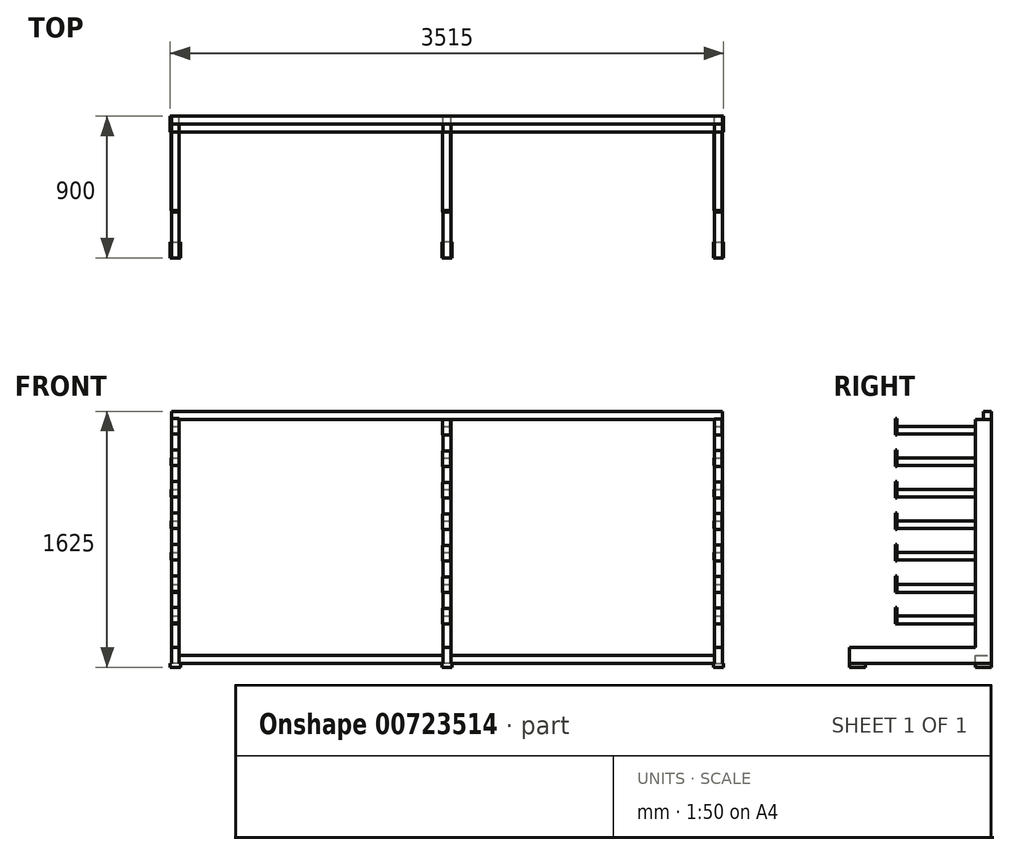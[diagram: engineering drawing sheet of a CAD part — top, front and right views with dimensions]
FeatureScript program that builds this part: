
annotation { "Feature Type Name" : "Feature", "Feature Type Description" : "" }
export const myFeature = defineFeature(function(context is Context, id is Id, definition is map)
    precondition{}
    {
        {
            var Q0;
            Q0=qCreatedBy(makeId("Front.planeOp"),FACE);
            var sketch = newSketch(context, id + "F0", { "sketchPlane" : qUnion([Q0])});
            skLineSegment(sketch, "E0.bottom", {"start": v(0, 0) * mm, "end": v(-3500, 0) * mm});
            skLineSegment(sketch, "E0.left", {"start": v(0, 0) * mm, "end": v(0, 1550) * mm});
            skLineSegment(sketch, "E0.right", {"start": v(-3500, 0) * mm, "end": v(-3500, 1550) * mm});
            skLineSegment(sketch, "E1.1", {"start": v(-50, 50) * mm, "end": v(-50, 1550) * mm});
            skLineSegment(sketch, "E1.2", {"start": v(-50, 50) * mm, "end": v(-1725, 50) * mm});
            skLineSegment(sketch, "E1.3", {"start": v(-3450, 50) * mm, "end": v(-3450, 1550) * mm});
            skPoint(sketch, "E2", {"position": v(-1775, 50) * mm});
            skPoint(sketch, "E3", {"position": v(-1725, 50) * mm});
            skLineSegment(sketch, "E4", {"start": v(-1775, 50) * mm, "end": v(-1775, 1550) * mm});
            skLineSegment(sketch, "E5.0", {"start": v(-1725, 50) * mm, "end": v(-1725, 1550) * mm});
            skLineSegment(sketch, "E6.trimOffspring", {"start": v(-1775, 50) * mm, "end": v(-3450, 50) * mm});
            skLineSegment(sketch, "E7", {"start": v(-3450, 1550) * mm, "end": v(-3500, 1550) * mm});
            skLineSegment(sketch, "E8", {"start": v(-1775, 1550) * mm, "end": v(-1725, 1550) * mm});
            skLineSegment(sketch, "E9", {"start": v(-50, 1550) * mm, "end": v(0, 1550) * mm});
            skSolve(sketch);
        }
        {
            var Q0;
            Q0=makeQuery(id+"F0.imprint","IMPRINT",FACE,{"disambiguationData":[TD([[makeQuery(id+"F0.imprint","IMPRINT",EDGE,{"derivedFrom":sQuery(id+"F0.wireOp",EDGE,"E0.bottom")}),-1.0]])]});
            extrude(context, id + "F1", {"entities" : qUnion([Q0]), "depth" : 100 * mm, "offsetDistance" : 25 * mm});
        }
        {
            var Q0;
            Q0=makeQuery(id+"F1.opExtrude","CAP_FACE",FACE,{"disambiguationData":[OSD([sQuery(id+"F0.wireOp",EDGE,"E0.bottom"),sQuery(id+"F0.wireOp",EDGE,"E0.left"),sQuery(id+"F0.wireOp",EDGE,"E0.right"),sQuery(id+"F0.wireOp",EDGE,"E1.1"),sQuery(id+"F0.wireOp",EDGE,"E1.2"),sQuery(id+"F0.wireOp",EDGE,"E1.3"),sQuery(id+"F0.wireOp",EDGE,"E4"),sQuery(id+"F0.wireOp",EDGE,"E5.0"),sQuery(id+"F0.wireOp",EDGE,"E6.trimOffspring"),sQuery(id+"F0.wireOp",EDGE,"E7"),sQuery(id+"F0.wireOp",EDGE,"E8"),sQuery(id+"F0.wireOp",EDGE,"E9")])],"isStart":false});
            var sketch = newSketch(context, id + "F2", { "sketchPlane" : qUnion([Q0])});
            skLineSegment(sketch, "E10.bottom", {"start": v(-3500, 0) * mm, "end": v(-3450, 0) * mm});
            skLineSegment(sketch, "E10.top", {"start": v(-3500, 100) * mm, "end": v(-3450, 100) * mm});
            skLineSegment(sketch, "E10.left", {"start": v(-3500, 0) * mm, "end": v(-3500, 100) * mm});
            skLineSegment(sketch, "E10.right", {"start": v(-3450, 0) * mm, "end": v(-3450, 100) * mm});
            skLineSegment(sketch, "E11.bottom", {"start": v(-1775, 0) * mm, "end": v(-1725, 0) * mm});
            skLineSegment(sketch, "E11.top", {"start": v(-1775, 100) * mm, "end": v(-1725, 100) * mm});
            skLineSegment(sketch, "E11.left", {"start": v(-1775, 0) * mm, "end": v(-1775, 100) * mm});
            skLineSegment(sketch, "E11.right", {"start": v(-1725, 0) * mm, "end": v(-1725, 100) * mm});
            skLineSegment(sketch, "E12.bottom", {"start": v(0, 0) * mm, "end": v(-50, 0) * mm});
            skLineSegment(sketch, "E12.top", {"start": v(0, 100) * mm, "end": v(-50, 100) * mm});
            skLineSegment(sketch, "E12.left", {"start": v(0, 0) * mm, "end": v(0, 100) * mm});
            skLineSegment(sketch, "E12.right", {"start": v(-50, 0) * mm, "end": v(-50, 100) * mm});
            skSolve(sketch);
        }
        {
            var Q0;
            {var subQ2=sQuery(id+"F2.wireOp",EDGE,"E11.bottom");Q0=makeQuery(id+"F2.imprint","IMPRINT",FACE,{"disambiguationData":[TD([[makeQuery(id+"F2.imprint","IMPRINT",EDGE,{"derivedFrom":subQ2}),-1.0]])]});}
            var Q1;
            {var subQ3=sQuery(id+"F2.wireOp",EDGE,"E10.bottom");Q1=makeQuery(id+"F2.imprint","IMPRINT",FACE,{"disambiguationData":[TD([[makeQuery(id+"F2.imprint","IMPRINT",EDGE,{"derivedFrom":subQ3}),-1.0]])]});}
            var Q2;
            {var subQ3=sQuery(id+"F2.wireOp",EDGE,"E12.bottom");Q2=makeQuery(id+"F2.imprint","IMPRINT",FACE,{"disambiguationData":[TD([[makeQuery(id+"F2.imprint","IMPRINT",EDGE,{"derivedFrom":subQ3}),-1.0]])]});}
            extrude(context, id + "F3", {"entities" : qUnion([Q0, Q1, Q2]), "operationType" : NewBodyOperationType.ADD, "depth" : 800 * mm, "offsetDistance" : 25 * mm});
        }
        {
            var Q0;
            Q0=makeQuery(id+"F1.opExtrude","SWEPT_FACE",FACE,{"disambiguationData":[OSD([sQuery(id+"F0.wireOp",EDGE,"E8")])]});
            var sketch = newSketch(context, id + "F4", { "sketchPlane" : qUnion([Q0])});
            skPoint(sketch, "E13", {"position": v(-1750, 0) * mm});
            skPoint(sketch, "E14", {"position": v(-1750, -100) * mm});
            skLineSegment(sketch, "E15", {"start": v(-1750, 0) * mm, "end": v(-1750, -50) * mm});
            skLineSegment(sketch, "E16.bottom", {"start": v(-1750, -50) * mm, "end": v(-3499.82, -50) * mm});
            skLineSegment(sketch, "E16.top", {"start": v(-1750, 0) * mm, "end": v(-3499.82, 0) * mm});
            skLineSegment(sketch, "E16.left", {"start": v(-1750, -50) * mm, "end": v(-1750, 0) * mm});
            skLineSegment(sketch, "E16.right", {"start": v(-3499.82, -50) * mm, "end": v(-3499.82, 0) * mm});
            skLineSegment(sketch, "E17.MirrorCS", {"start": v(-1750, 0) * mm, "end": v(-0.18, 0) * mm});
            skLineSegment(sketch, "E18.MirrorCS", {"start": v(-1750, -50) * mm, "end": v(-0.18, -50) * mm});
            skLineSegment(sketch, "E19.MirrorCS", {"start": v(-0.18, -50) * mm, "end": v(-0.18, 0) * mm});
            skSolve(sketch);
        }
        {
            var Q0;
            Q0 = qSketchRegion(id + "F4", true);
            extrude(context, id + "F5", {"entities" : qUnion([Q0]), "operationType" : NewBodyOperationType.ADD, "depth" : 50 * mm, "offsetDistance" : 25 * mm});
        }
        {
            var Q0;
            {var subQ0=sQuery(id+"F0.wireOp",EDGE,"E0.right");var subQ1=sQuery(id+"F0.wireOp",EDGE,"E7");var subQ2=sQuery(id+"F0.wireOp",EDGE,"E1.3");Q0=makeQuery(id+"F3.boolean.opBoolean","SPLIT",FACE,{"disambiguationData":[TD([makeQuery(id+"F1.opExtrude","SWEPT_FACE",FACE,{"disambiguationData":[OSD([subQ0])]})])],"derivedFrom":makeQuery(id+"F1.opExtrude","CAP_FACE",FACE,{"disambiguationData":[OSD([sQuery(id+"F0.wireOp",EDGE,"E0.bottom"),sQuery(id+"F0.wireOp",EDGE,"E0.left"),subQ0,sQuery(id+"F0.wireOp",EDGE,"E1.1"),sQuery(id+"F0.wireOp",EDGE,"E1.2"),subQ2,sQuery(id+"F0.wireOp",EDGE,"E4"),sQuery(id+"F0.wireOp",EDGE,"E5.0"),sQuery(id+"F0.wireOp",EDGE,"E6.trimOffspring"),subQ1,sQuery(id+"F0.wireOp",EDGE,"E8"),sQuery(id+"F0.wireOp",EDGE,"E9")])],"isStart":false})});}
            var sketch = newSketch(context, id + "F6", { "sketchPlane" : qUnion([Q0])});
            skLineSegment(sketch, "E20.bottom", {"start": v(-3500, 250) * mm, "end": v(-3450, 250) * mm});
            skLineSegment(sketch, "E20.top", {"start": v(-3500, 300) * mm, "end": v(-3450, 300) * mm});
            skLineSegment(sketch, "E20.left", {"start": v(-3500, 250) * mm, "end": v(-3500, 300) * mm});
            skLineSegment(sketch, "E20.right", {"start": v(-3450, 250) * mm, "end": v(-3450, 300) * mm});
            skPoint(sketch, "E21", {"position": v(-3500, 450) * mm});
            skLineSegment(sketch, "E22.bottom", {"start": v(-3500, 450) * mm, "end": v(-3450, 450) * mm});
            skLineSegment(sketch, "E22.top", {"start": v(-3500, 500) * mm, "end": v(-3450, 500) * mm});
            skLineSegment(sketch, "E22.left", {"start": v(-3500, 450) * mm, "end": v(-3500, 500) * mm});
            skLineSegment(sketch, "E22.right", {"start": v(-3450, 450) * mm, "end": v(-3450, 500) * mm});
            skPoint(sketch, "E23", {"position": v(-3500, 650) * mm});
            skPoint(sketch, "E24", {"position": v(-3500.84, 655.24) * mm});
            skPoint(sketch, "E25", {"position": v(-3500.84, 855.24) * mm});
            skPoint(sketch, "E26", {"position": v(-3500.84, 1055.24) * mm});
            skPoint(sketch, "E27", {"position": v(-3500.84, 1255.24) * mm});
            skLineSegment(sketch, "E28.bottom", {"start": v(-3500.84, 655.24) * mm, "end": v(-3450.84, 655.24) * mm});
            skLineSegment(sketch, "E28.top", {"start": v(-3500.84, 705.24) * mm, "end": v(-3450.84, 705.24) * mm});
            skLineSegment(sketch, "E28.left", {"start": v(-3500.84, 655.24) * mm, "end": v(-3500.84, 705.24) * mm});
            skLineSegment(sketch, "E28.right", {"start": v(-3450.84, 655.24) * mm, "end": v(-3450.84, 705.24) * mm});
            skLineSegment(sketch, "E29.bottom", {"start": v(-3500.84, 855.24) * mm, "end": v(-3450.84, 855.24) * mm});
            skLineSegment(sketch, "E29.top", {"start": v(-3500.84, 905.24) * mm, "end": v(-3450.84, 905.24) * mm});
            skLineSegment(sketch, "E29.left", {"start": v(-3500.84, 855.24) * mm, "end": v(-3500.84, 905.24) * mm});
            skLineSegment(sketch, "E29.right", {"start": v(-3450.84, 855.24) * mm, "end": v(-3450.84, 905.24) * mm});
            skLineSegment(sketch, "E30.bottom", {"start": v(-3500.84, 1055.24) * mm, "end": v(-3450.84, 1055.24) * mm});
            skLineSegment(sketch, "E30.top", {"start": v(-3500.84, 1105.24) * mm, "end": v(-3450.84, 1105.24) * mm});
            skLineSegment(sketch, "E30.left", {"start": v(-3500.84, 1055.24) * mm, "end": v(-3500.84, 1105.24) * mm});
            skLineSegment(sketch, "E30.right", {"start": v(-3450.84, 1055.24) * mm, "end": v(-3450.84, 1105.24) * mm});
            skLineSegment(sketch, "E31.bottom", {"start": v(-3500.84, 1255.24) * mm, "end": v(-3450.84, 1255.24) * mm});
            skLineSegment(sketch, "E31.top", {"start": v(-3500.84, 1305.24) * mm, "end": v(-3450.84, 1305.24) * mm});
            skLineSegment(sketch, "E31.left", {"start": v(-3500.84, 1255.24) * mm, "end": v(-3500.84, 1305.24) * mm});
            skLineSegment(sketch, "E31.right", {"start": v(-3450.84, 1255.24) * mm, "end": v(-3450.84, 1305.24) * mm});
            skPoint(sketch, "E32", {"position": v(-3500, 1455.24) * mm});
            skLineSegment(sketch, "E33.bottom", {"start": v(-3500, 1455.24) * mm, "end": v(-3450, 1455.24) * mm});
            skLineSegment(sketch, "E33.top", {"start": v(-3500, 1505.24) * mm, "end": v(-3450, 1505.24) * mm});
            skLineSegment(sketch, "E33.left", {"start": v(-3500, 1455.24) * mm, "end": v(-3500, 1505.24) * mm});
            skLineSegment(sketch, "E33.right", {"start": v(-3450, 1455.24) * mm, "end": v(-3450, 1505.24) * mm});
            skPoint(sketch, "E34", {"position": v(-52.24, 250) * mm});
            skPoint(sketch, "E35", {"position": v(-1777.89, 250) * mm});
            skLineSegment(sketch, "E36.bottom", {"start": v(-1777.89, 250) * mm, "end": v(-1727.89, 250) * mm});
            skLineSegment(sketch, "E36.top", {"start": v(-1777.89, 300) * mm, "end": v(-1727.89, 300) * mm});
            skLineSegment(sketch, "E36.left", {"start": v(-1777.89, 250) * mm, "end": v(-1777.89, 300) * mm});
            skLineSegment(sketch, "E36.right", {"start": v(-1727.89, 250) * mm, "end": v(-1727.89, 300) * mm});
            skPoint(sketch, "E37", {"position": v(-1777.89, 450) * mm});
            skLineSegment(sketch, "E38.bottom", {"start": v(-1777.89, 450) * mm, "end": v(-1727.89, 450) * mm});
            skLineSegment(sketch, "E38.top", {"start": v(-1777.89, 500) * mm, "end": v(-1727.89, 500) * mm});
            skLineSegment(sketch, "E38.left", {"start": v(-1777.89, 450) * mm, "end": v(-1777.89, 500) * mm});
            skLineSegment(sketch, "E38.right", {"start": v(-1727.89, 450) * mm, "end": v(-1727.89, 500) * mm});
            skPoint(sketch, "E39", {"position": v(-1777.89, 650) * mm});
            skPoint(sketch, "E40", {"position": v(-1778.73, 655.24) * mm});
            skPoint(sketch, "E41", {"position": v(-1778.73, 855.24) * mm});
            skPoint(sketch, "E42", {"position": v(-1778.73, 1055.24) * mm});
            skPoint(sketch, "E43", {"position": v(-1778.73, 1255.24) * mm});
            skLineSegment(sketch, "E44.bottom", {"start": v(-1778.73, 655.24) * mm, "end": v(-1728.73, 655.24) * mm});
            skLineSegment(sketch, "E44.top", {"start": v(-1778.73, 705.24) * mm, "end": v(-1728.73, 705.24) * mm});
            skLineSegment(sketch, "E44.left", {"start": v(-1778.73, 655.24) * mm, "end": v(-1778.73, 705.24) * mm});
            skLineSegment(sketch, "E44.right", {"start": v(-1728.73, 655.24) * mm, "end": v(-1728.73, 705.24) * mm});
            skLineSegment(sketch, "E45.bottom", {"start": v(-1778.73, 855.24) * mm, "end": v(-1728.73, 855.24) * mm});
            skLineSegment(sketch, "E45.top", {"start": v(-1778.73, 905.24) * mm, "end": v(-1728.73, 905.24) * mm});
            skLineSegment(sketch, "E45.left", {"start": v(-1778.73, 855.24) * mm, "end": v(-1778.73, 905.24) * mm});
            skLineSegment(sketch, "E45.right", {"start": v(-1728.73, 855.24) * mm, "end": v(-1728.73, 905.24) * mm});
            skLineSegment(sketch, "E46.bottom", {"start": v(-1778.73, 1055.24) * mm, "end": v(-1728.73, 1055.24) * mm});
            skLineSegment(sketch, "E46.top", {"start": v(-1778.73, 1105.24) * mm, "end": v(-1728.73, 1105.24) * mm});
            skLineSegment(sketch, "E46.left", {"start": v(-1778.73, 1055.24) * mm, "end": v(-1778.73, 1105.24) * mm});
            skLineSegment(sketch, "E46.right", {"start": v(-1728.73, 1055.24) * mm, "end": v(-1728.73, 1105.24) * mm});
            skLineSegment(sketch, "E47.bottom", {"start": v(-1778.73, 1255.24) * mm, "end": v(-1728.73, 1255.24) * mm});
            skLineSegment(sketch, "E47.top", {"start": v(-1778.73, 1305.24) * mm, "end": v(-1728.73, 1305.24) * mm});
            skLineSegment(sketch, "E47.left", {"start": v(-1778.73, 1255.24) * mm, "end": v(-1778.73, 1305.24) * mm});
            skLineSegment(sketch, "E47.right", {"start": v(-1728.73, 1255.24) * mm, "end": v(-1728.73, 1305.24) * mm});
            skPoint(sketch, "E48", {"position": v(-1777.89, 1455.24) * mm});
            skLineSegment(sketch, "E49.bottom", {"start": v(-1777.89, 1455.24) * mm, "end": v(-1727.89, 1455.24) * mm});
            skLineSegment(sketch, "E49.top", {"start": v(-1777.89, 1505.24) * mm, "end": v(-1727.89, 1505.24) * mm});
            skLineSegment(sketch, "E49.left", {"start": v(-1777.89, 1455.24) * mm, "end": v(-1777.89, 1505.24) * mm});
            skLineSegment(sketch, "E49.right", {"start": v(-1727.89, 1455.24) * mm, "end": v(-1727.89, 1505.24) * mm});
            skLineSegment(sketch, "E50.bottom", {"start": v(-52.24, 250) * mm, "end": v(-2.24, 250) * mm});
            skLineSegment(sketch, "E50.top", {"start": v(-52.24, 300) * mm, "end": v(-2.24, 300) * mm});
            skLineSegment(sketch, "E50.left", {"start": v(-52.24, 250) * mm, "end": v(-52.24, 300) * mm});
            skLineSegment(sketch, "E50.right", {"start": v(-2.24, 250) * mm, "end": v(-2.24, 300) * mm});
            skPoint(sketch, "E51", {"position": v(-52.24, 450) * mm});
            skLineSegment(sketch, "E52.bottom", {"start": v(-52.24, 450) * mm, "end": v(-2.24, 450) * mm});
            skLineSegment(sketch, "E52.top", {"start": v(-52.24, 500) * mm, "end": v(-2.24, 500) * mm});
            skLineSegment(sketch, "E52.left", {"start": v(-52.24, 450) * mm, "end": v(-52.24, 500) * mm});
            skLineSegment(sketch, "E52.right", {"start": v(-2.24, 450) * mm, "end": v(-2.24, 500) * mm});
            skPoint(sketch, "E53", {"position": v(-52.24, 650) * mm});
            skPoint(sketch, "E54", {"position": v(-53.08, 655.24) * mm});
            skPoint(sketch, "E55", {"position": v(-53.08, 855.24) * mm});
            skPoint(sketch, "E56", {"position": v(-53.08, 1055.24) * mm});
            skPoint(sketch, "E57", {"position": v(-53.08, 1255.24) * mm});
            skLineSegment(sketch, "E58.bottom", {"start": v(-53.08, 655.24) * mm, "end": v(-3.08, 655.24) * mm});
            skLineSegment(sketch, "E58.top", {"start": v(-53.08, 705.24) * mm, "end": v(-3.08, 705.24) * mm});
            skLineSegment(sketch, "E58.left", {"start": v(-53.08, 655.24) * mm, "end": v(-53.08, 705.24) * mm});
            skLineSegment(sketch, "E58.right", {"start": v(-3.08, 655.24) * mm, "end": v(-3.08, 705.24) * mm});
            skLineSegment(sketch, "E59.bottom", {"start": v(-53.08, 855.24) * mm, "end": v(-3.08, 855.24) * mm});
            skLineSegment(sketch, "E59.top", {"start": v(-53.08, 905.24) * mm, "end": v(-3.08, 905.24) * mm});
            skLineSegment(sketch, "E59.left", {"start": v(-53.08, 855.24) * mm, "end": v(-53.08, 905.24) * mm});
            skLineSegment(sketch, "E59.right", {"start": v(-3.08, 855.24) * mm, "end": v(-3.08, 905.24) * mm});
            skLineSegment(sketch, "E60.bottom", {"start": v(-53.08, 1055.24) * mm, "end": v(-3.08, 1055.24) * mm});
            skLineSegment(sketch, "E60.top", {"start": v(-53.08, 1105.24) * mm, "end": v(-3.08, 1105.24) * mm});
            skLineSegment(sketch, "E60.left", {"start": v(-53.08, 1055.24) * mm, "end": v(-53.08, 1105.24) * mm});
            skLineSegment(sketch, "E60.right", {"start": v(-3.08, 1055.24) * mm, "end": v(-3.08, 1105.24) * mm});
            skLineSegment(sketch, "E61.bottom", {"start": v(-53.08, 1255.24) * mm, "end": v(-3.08, 1255.24) * mm});
            skLineSegment(sketch, "E61.top", {"start": v(-53.08, 1305.24) * mm, "end": v(-3.08, 1305.24) * mm});
            skLineSegment(sketch, "E61.left", {"start": v(-53.08, 1255.24) * mm, "end": v(-53.08, 1305.24) * mm});
            skLineSegment(sketch, "E61.right", {"start": v(-3.08, 1255.24) * mm, "end": v(-3.08, 1305.24) * mm});
            skPoint(sketch, "E62", {"position": v(-52.24, 1455.24) * mm});
            skLineSegment(sketch, "E63.bottom", {"start": v(-52.24, 1455.24) * mm, "end": v(-2.24, 1455.24) * mm});
            skLineSegment(sketch, "E63.top", {"start": v(-52.24, 1505.24) * mm, "end": v(-2.24, 1505.24) * mm});
            skLineSegment(sketch, "E63.left", {"start": v(-52.24, 1455.24) * mm, "end": v(-52.24, 1505.24) * mm});
            skLineSegment(sketch, "E63.right", {"start": v(-2.24, 1455.24) * mm, "end": v(-2.24, 1505.24) * mm});
            skSolve(sketch);
        }
        {
            var Q0;
            Q0 = qSketchRegion(id + "F6", true);
            extrude(context, id + "F7", {"entities" : qUnion([Q0]), "operationType" : NewBodyOperationType.ADD, "depth" : 500 * mm, "offsetDistance" : 25 * mm});
        }
        {
            var Q0;
            Q0=makeQuery(id+"F7.opExtrude","CAP_FACE",FACE,{"disambiguationData":[OSD([sQuery(id+"F6.wireOp",EDGE,"E33.bottom"),sQuery(id+"F6.wireOp",EDGE,"E33.top"),sQuery(id+"F6.wireOp",EDGE,"E33.left"),sQuery(id+"F6.wireOp",EDGE,"E33.right")])],"isStart":false});
            var sketch = newSketch(context, id + "F8", { "sketchPlane" : qUnion([Q0])});
            skLineSegment(sketch, "E64.bottom", {"start": v(-3500, 1455.24) * mm, "end": v(-3450, 1455.24) * mm});
            skLineSegment(sketch, "E64.top", {"start": v(-3500, 1555.24) * mm, "end": v(-3450, 1555.24) * mm});
            skLineSegment(sketch, "E64.left", {"start": v(-3500, 1455.24) * mm, "end": v(-3500, 1555.24) * mm});
            skLineSegment(sketch, "E64.right", {"start": v(-3450, 1455.24) * mm, "end": v(-3450, 1555.24) * mm});
            skLineSegment(sketch, "E65.0.1.0", {"start": v(-3500, 1355.24) * mm, "end": v(-3450, 1355.24) * mm});
            skLineSegment(sketch, "E65.0.1.1", {"start": v(-3450, 1255.24) * mm, "end": v(-3450, 1355.24) * mm});
            skLineSegment(sketch, "E65.0.1.2", {"start": v(-3500, 1255.24) * mm, "end": v(-3450, 1255.24) * mm});
            skLineSegment(sketch, "E65.0.1.3", {"start": v(-3500, 1255.24) * mm, "end": v(-3500, 1355.24) * mm});
            skLineSegment(sketch, "E65.0.2.0", {"start": v(-3500, 1155.24) * mm, "end": v(-3450, 1155.24) * mm});
            skLineSegment(sketch, "E65.0.2.1", {"start": v(-3450, 1055.24) * mm, "end": v(-3450, 1155.24) * mm});
            skLineSegment(sketch, "E65.0.2.2", {"start": v(-3500, 1055.24) * mm, "end": v(-3450, 1055.24) * mm});
            skLineSegment(sketch, "E65.0.2.3", {"start": v(-3500, 1055.24) * mm, "end": v(-3500, 1155.24) * mm});
            skLineSegment(sketch, "E65.0.3.0", {"start": v(-3500, 955.24) * mm, "end": v(-3450, 955.24) * mm});
            skLineSegment(sketch, "E65.0.3.1", {"start": v(-3450, 855.24) * mm, "end": v(-3450, 955.24) * mm});
            skLineSegment(sketch, "E65.0.3.2", {"start": v(-3500, 855.24) * mm, "end": v(-3450, 855.24) * mm});
            skLineSegment(sketch, "E65.0.3.3", {"start": v(-3500, 855.24) * mm, "end": v(-3500, 955.24) * mm});
            skLineSegment(sketch, "E65.0.4.0", {"start": v(-3500, 755.24) * mm, "end": v(-3450, 755.24) * mm});
            skLineSegment(sketch, "E65.0.4.1", {"start": v(-3450, 655.24) * mm, "end": v(-3450, 755.24) * mm});
            skLineSegment(sketch, "E65.0.4.2", {"start": v(-3500, 655.24) * mm, "end": v(-3450, 655.24) * mm});
            skLineSegment(sketch, "E65.0.4.3", {"start": v(-3500, 655.24) * mm, "end": v(-3500, 755.24) * mm});
            skLineSegment(sketch, "E65.0.5.0", {"start": v(-3500, 555.24) * mm, "end": v(-3450, 555.24) * mm});
            skLineSegment(sketch, "E65.0.5.1", {"start": v(-3450, 455.24) * mm, "end": v(-3450, 555.24) * mm});
            skLineSegment(sketch, "E65.0.5.2", {"start": v(-3500, 455.24) * mm, "end": v(-3450, 455.24) * mm});
            skLineSegment(sketch, "E65.0.5.3", {"start": v(-3500, 455.24) * mm, "end": v(-3500, 555.24) * mm});
            skLineSegment(sketch, "E65.0.6.0", {"start": v(-3500, 355.24) * mm, "end": v(-3450, 355.24) * mm});
            skLineSegment(sketch, "E65.0.6.1", {"start": v(-3450, 255.24) * mm, "end": v(-3450, 355.24) * mm});
            skLineSegment(sketch, "E65.0.6.2", {"start": v(-3500, 255.24) * mm, "end": v(-3450, 255.24) * mm});
            skLineSegment(sketch, "E65.0.6.3", {"start": v(-3500, 255.24) * mm, "end": v(-3500, 355.24) * mm});
            skLineSegment(sketch, "E65.direction1", {"start": v(-3500, 1455.24) * mm, "end": v(-3475, 1455.24) * mm, "construction": true});
            skLineSegment(sketch, "E65.direction2", {"start": v(-3500, 1455.24) * mm, "end": v(-3500, 1255.24) * mm, "construction": true});
            skLineSegment(sketch, "E66.bottom", {"start": v(-1778.75, 1448.92) * mm, "end": v(-1728.75, 1448.92) * mm});
            skLineSegment(sketch, "E66.top", {"start": v(-1778.75, 1548.92) * mm, "end": v(-1728.75, 1548.92) * mm});
            skLineSegment(sketch, "E66.left", {"start": v(-1778.75, 1448.92) * mm, "end": v(-1778.75, 1548.92) * mm});
            skLineSegment(sketch, "E66.right", {"start": v(-1728.75, 1448.92) * mm, "end": v(-1728.75, 1548.92) * mm});
            skLineSegment(sketch, "E67.0.1.0", {"start": v(-1778.75, 1348.92) * mm, "end": v(-1728.75, 1348.92) * mm});
            skLineSegment(sketch, "E67.0.1.1", {"start": v(-1728.75, 1248.92) * mm, "end": v(-1728.75, 1348.92) * mm});
            skLineSegment(sketch, "E67.0.1.2", {"start": v(-1778.75, 1248.92) * mm, "end": v(-1728.75, 1248.92) * mm});
            skLineSegment(sketch, "E67.0.1.3", {"start": v(-1778.75, 1248.92) * mm, "end": v(-1778.75, 1348.92) * mm});
            skLineSegment(sketch, "E67.0.2.0", {"start": v(-1778.75, 1148.92) * mm, "end": v(-1728.75, 1148.92) * mm});
            skLineSegment(sketch, "E67.0.2.1", {"start": v(-1728.75, 1048.92) * mm, "end": v(-1728.75, 1148.92) * mm});
            skLineSegment(sketch, "E67.0.2.2", {"start": v(-1778.75, 1048.92) * mm, "end": v(-1728.75, 1048.92) * mm});
            skLineSegment(sketch, "E67.0.2.3", {"start": v(-1778.75, 1048.92) * mm, "end": v(-1778.75, 1148.92) * mm});
            skLineSegment(sketch, "E67.0.3.0", {"start": v(-1778.75, 948.92) * mm, "end": v(-1728.75, 948.92) * mm});
            skLineSegment(sketch, "E67.0.3.1", {"start": v(-1728.75, 848.92) * mm, "end": v(-1728.75, 948.92) * mm});
            skLineSegment(sketch, "E67.0.3.2", {"start": v(-1778.75, 848.92) * mm, "end": v(-1728.75, 848.92) * mm});
            skLineSegment(sketch, "E67.0.3.3", {"start": v(-1778.75, 848.92) * mm, "end": v(-1778.75, 948.92) * mm});
            skLineSegment(sketch, "E67.0.4.0", {"start": v(-1778.75, 748.92) * mm, "end": v(-1728.75, 748.92) * mm});
            skLineSegment(sketch, "E67.0.4.1", {"start": v(-1728.75, 648.92) * mm, "end": v(-1728.75, 748.92) * mm});
            skLineSegment(sketch, "E67.0.4.2", {"start": v(-1778.75, 648.92) * mm, "end": v(-1728.75, 648.92) * mm});
            skLineSegment(sketch, "E67.0.4.3", {"start": v(-1778.75, 648.92) * mm, "end": v(-1778.75, 748.92) * mm});
            skLineSegment(sketch, "E67.0.5.0", {"start": v(-1778.75, 548.92) * mm, "end": v(-1728.75, 548.92) * mm});
            skLineSegment(sketch, "E67.0.5.1", {"start": v(-1728.75, 448.92) * mm, "end": v(-1728.75, 548.92) * mm});
            skLineSegment(sketch, "E67.0.5.2", {"start": v(-1778.75, 448.92) * mm, "end": v(-1728.75, 448.92) * mm});
            skLineSegment(sketch, "E67.0.5.3", {"start": v(-1778.75, 448.92) * mm, "end": v(-1778.75, 548.92) * mm});
            skLineSegment(sketch, "E67.0.6.0", {"start": v(-1778.75, 348.92) * mm, "end": v(-1728.75, 348.92) * mm});
            skLineSegment(sketch, "E67.0.6.1", {"start": v(-1728.75, 248.92) * mm, "end": v(-1728.75, 348.92) * mm});
            skLineSegment(sketch, "E67.0.6.2", {"start": v(-1778.75, 248.92) * mm, "end": v(-1728.75, 248.92) * mm});
            skLineSegment(sketch, "E67.0.6.3", {"start": v(-1778.75, 248.92) * mm, "end": v(-1778.75, 348.92) * mm});
            skLineSegment(sketch, "E67.direction1", {"start": v(-1778.75, 1448.92) * mm, "end": v(-1753.75, 1448.92) * mm, "construction": true});
            skLineSegment(sketch, "E67.direction2", {"start": v(-1778.75, 1448.92) * mm, "end": v(-1778.75, 1248.92) * mm, "construction": true});
            skLineSegment(sketch, "E68.bottom", {"start": v(-52, 1450.5) * mm, "end": v(-2, 1450.5) * mm});
            skLineSegment(sketch, "E68.top", {"start": v(-52, 1550.5) * mm, "end": v(-2, 1550.5) * mm});
            skLineSegment(sketch, "E68.left", {"start": v(-52, 1450.5) * mm, "end": v(-52, 1550.5) * mm});
            skLineSegment(sketch, "E68.right", {"start": v(-2, 1450.5) * mm, "end": v(-2, 1550.5) * mm});
            skLineSegment(sketch, "E69.0.1.0", {"start": v(-52, 1350.5) * mm, "end": v(-2, 1350.5) * mm});
            skLineSegment(sketch, "E69.0.1.1", {"start": v(-2, 1250.5) * mm, "end": v(-2, 1350.5) * mm});
            skLineSegment(sketch, "E69.0.1.2", {"start": v(-52, 1250.5) * mm, "end": v(-2, 1250.5) * mm});
            skLineSegment(sketch, "E69.0.1.3", {"start": v(-52, 1250.5) * mm, "end": v(-52, 1350.5) * mm});
            skLineSegment(sketch, "E69.0.2.0", {"start": v(-52, 1150.5) * mm, "end": v(-2, 1150.5) * mm});
            skLineSegment(sketch, "E69.0.2.1", {"start": v(-2, 1050.5) * mm, "end": v(-2, 1150.5) * mm});
            skLineSegment(sketch, "E69.0.2.2", {"start": v(-52, 1050.5) * mm, "end": v(-2, 1050.5) * mm});
            skLineSegment(sketch, "E69.0.2.3", {"start": v(-52, 1050.5) * mm, "end": v(-52, 1150.5) * mm});
            skLineSegment(sketch, "E69.0.3.0", {"start": v(-52, 950.5) * mm, "end": v(-2, 950.5) * mm});
            skLineSegment(sketch, "E69.0.3.1", {"start": v(-2, 850.5) * mm, "end": v(-2, 950.5) * mm});
            skLineSegment(sketch, "E69.0.3.2", {"start": v(-52, 850.5) * mm, "end": v(-2, 850.5) * mm});
            skLineSegment(sketch, "E69.0.3.3", {"start": v(-52, 850.5) * mm, "end": v(-52, 950.5) * mm});
            skLineSegment(sketch, "E69.0.4.0", {"start": v(-52, 750.5) * mm, "end": v(-2, 750.5) * mm});
            skLineSegment(sketch, "E69.0.4.1", {"start": v(-2, 650.5) * mm, "end": v(-2, 750.5) * mm});
            skLineSegment(sketch, "E69.0.4.2", {"start": v(-52, 650.5) * mm, "end": v(-2, 650.5) * mm});
            skLineSegment(sketch, "E69.0.4.3", {"start": v(-52, 650.5) * mm, "end": v(-52, 750.5) * mm});
            skLineSegment(sketch, "E69.0.5.0", {"start": v(-52, 550.5) * mm, "end": v(-2, 550.5) * mm});
            skLineSegment(sketch, "E69.0.5.1", {"start": v(-2, 450.5) * mm, "end": v(-2, 550.5) * mm});
            skLineSegment(sketch, "E69.0.5.2", {"start": v(-52, 450.5) * mm, "end": v(-2, 450.5) * mm});
            skLineSegment(sketch, "E69.0.5.3", {"start": v(-52, 450.5) * mm, "end": v(-52, 550.5) * mm});
            skLineSegment(sketch, "E69.0.6.0", {"start": v(-52, 350.5) * mm, "end": v(-2, 350.5) * mm});
            skLineSegment(sketch, "E69.0.6.1", {"start": v(-2, 250.5) * mm, "end": v(-2, 350.5) * mm});
            skLineSegment(sketch, "E69.0.6.2", {"start": v(-52, 250.5) * mm, "end": v(-2, 250.5) * mm});
            skLineSegment(sketch, "E69.0.6.3", {"start": v(-52, 250.5) * mm, "end": v(-52, 350.5) * mm});
            skLineSegment(sketch, "E69.direction1", {"start": v(-52, 1450.5) * mm, "end": v(-27, 1450.5) * mm, "construction": true});
            skLineSegment(sketch, "E69.direction2", {"start": v(-52, 1450.5) * mm, "end": v(-52, 1250.5) * mm, "construction": true});
            skSolve(sketch);
        }
        {
            var Q0;
            Q0 = qSketchRegion(id + "F8", true);
            extrude(context, id + "F9", {"entities" : qUnion([Q0]), "operationType" : NewBodyOperationType.ADD, "depth" : 10 * mm, "offsetDistance" : 25 * mm});
        }
        {
            var Q0;
            Q0 = qSketchRegion(id + "F8", true);
            extrude(context, id + "F10", {"entities" : qUnion([Q0]), "operationType" : NewBodyOperationType.ADD, "depth" : 10 * mm, "offsetDistance" : 25 * mm});
        }
        {
            var Q0;
            Q0=makeQuery(id+"F3.boolean.opBoolean","MERGE",FACE,{"derivedFrom":[makeQuery(id+"F1.opExtrude","SWEPT_FACE",FACE,{"disambiguationData":[OSD([sQuery(id+"F0.wireOp",EDGE,"E0.bottom")])]}),makeQuery(id+"F3.opExtrude","SWEPT_FACE",FACE,{"disambiguationData":[OSD([sQuery(id+"F2.wireOp",EDGE,"E10.bottom")])]}),makeQuery(id+"F3.opExtrude","SWEPT_FACE",FACE,{"disambiguationData":[OSD([sQuery(id+"F2.wireOp",EDGE,"E11.bottom")])]}),makeQuery(id+"F3.opExtrude","SWEPT_FACE",FACE,{"disambiguationData":[OSD([sQuery(id+"F2.wireOp",EDGE,"E12.bottom")])]})]});
            var sketch = newSketch(context, id + "F11", { "sketchPlane" : qUnion([Q0])});
            skLineSegment(sketch, "E70", {"start": v(-3475, 900) * mm, "end": v(-3475, 800) * mm});
            skLineSegment(sketch, "E71.bottom", {"start": v(-3507.5, 800) * mm, "end": v(-3442.5, 800) * mm});
            skLineSegment(sketch, "E71.top", {"start": v(-3507.5, 900) * mm, "end": v(-3442.5, 900) * mm});
            skLineSegment(sketch, "E71.left", {"start": v(-3507.5, 800) * mm, "end": v(-3507.5, 900) * mm});
            skLineSegment(sketch, "E71.right", {"start": v(-3442.5, 800) * mm, "end": v(-3442.5, 900) * mm});
            skPoint(sketch, "E71.middle", {"position": v(-3475, 850) * mm});
            skPoint(sketch, "E72.MirrorP", {"position": v(-3475, 50) * mm});
            skLineSegment(sketch, "E73.MirrorCS", {"start": v(-3442.5, 100) * mm, "end": v(-3442.5, 0) * mm});
            skLineSegment(sketch, "E74.MirrorCS", {"start": v(-3475, 0) * mm, "end": v(-3475, 100) * mm});
            skLineSegment(sketch, "E75.MirrorCS", {"start": v(-3507.5, 100) * mm, "end": v(-3442.5, 100) * mm});
            skLineSegment(sketch, "E76.MirrorCS", {"start": v(-3507.5, 100) * mm, "end": v(-3507.5, 0) * mm});
            skLineSegment(sketch, "E77.MirrorCS", {"start": v(-3507.5, 0) * mm, "end": v(-3442.5, 0) * mm});
            skLineSegment(sketch, "E78", {"start": v(-1750, 900) * mm, "end": v(-1750, 0) * mm});
            skLineSegment(sketch, "E79.MirrorCS", {"start": v(-1717.5, 100) * mm, "end": v(-1782.5, 100) * mm});
            skPoint(sketch, "E80.MirrorP", {"position": v(-1750, 50) * mm});
            skLineSegment(sketch, "E81.MirrorCS", {"start": v(-1782.5, 100) * mm, "end": v(-1782.5, 0) * mm});
            skLineSegment(sketch, "E82.MirrorCS", {"start": v(-1750, 0) * mm, "end": v(-1750, 100) * mm});
            skLineSegment(sketch, "E83.MirrorCS", {"start": v(-1717.5, 0) * mm, "end": v(-1782.5, 0) * mm});
            skLineSegment(sketch, "E84.MirrorCS", {"start": v(-1717.5, 100) * mm, "end": v(-1717.5, 0) * mm});
            skLineSegment(sketch, "E85.MirrorCS", {"start": v(-1750, 900) * mm, "end": v(-1750, 800) * mm});
            skLineSegment(sketch, "E86.MirrorCS", {"start": v(-1717.5, 800) * mm, "end": v(-1782.5, 800) * mm});
            skLineSegment(sketch, "E87.MirrorCS", {"start": v(-1717.5, 900) * mm, "end": v(-1782.5, 900) * mm});
            skLineSegment(sketch, "E88.MirrorCS", {"start": v(-1717.5, 800) * mm, "end": v(-1717.5, 900) * mm});
            skPoint(sketch, "E89.MirrorP", {"position": v(-1750, 850) * mm});
            skLineSegment(sketch, "E90.MirrorCS", {"start": v(-1782.5, 800) * mm, "end": v(-1782.5, 900) * mm});
            skLineSegment(sketch, "E91", {"start": v(-25, 900) * mm, "end": v(-25, 0) * mm});
            skLineSegment(sketch, "E92.MirrorCS", {"start": v(-57.5, 800) * mm, "end": v(7.5, 800) * mm});
            skLineSegment(sketch, "E93.MirrorCS", {"start": v(-25, 900) * mm, "end": v(-25, 800) * mm});
            skPoint(sketch, "E94.MirrorP", {"position": v(-25, 850) * mm});
            skLineSegment(sketch, "E95.MirrorCS", {"start": v(7.5, 800) * mm, "end": v(7.5, 900) * mm});
            skLineSegment(sketch, "E96.MirrorCS", {"start": v(-57.5, 900) * mm, "end": v(7.5, 900) * mm});
            skLineSegment(sketch, "E97.MirrorCS", {"start": v(-57.5, 800) * mm, "end": v(-57.5, 900) * mm});
            skLineSegment(sketch, "E98.MirrorCS", {"start": v(-25, 0) * mm, "end": v(-25, 100) * mm});
            skLineSegment(sketch, "E99.MirrorCS", {"start": v(7.5, 100) * mm, "end": v(7.5, 0) * mm});
            skLineSegment(sketch, "E100.MirrorCS", {"start": v(-57.5, 100) * mm, "end": v(7.5, 100) * mm});
            skLineSegment(sketch, "E101.MirrorCS", {"start": v(-57.5, 100) * mm, "end": v(-57.5, 0) * mm});
            skPoint(sketch, "E102.MirrorP", {"position": v(-25, 50) * mm});
            skLineSegment(sketch, "E103.MirrorCS", {"start": v(-57.5, 0) * mm, "end": v(7.5, 0) * mm});
            skSolve(sketch);
        }
        {
            var Q0;
            Q0 = qSketchRegion(id + "F11", true);
            extrude(context, id + "F12", {"entities" : qUnion([Q0]), "operationType" : NewBodyOperationType.ADD, "depth" : 25 * mm, "offsetDistance" : 25 * mm});
        }
    });
